# Revit family: RN 41133 Rubinetto da giardino
name_source: partatom
category: Rohrzubehör
units: mm (PartAtom-declared; Revit-internal decimal feet)

## family parameters
Arbeitsebenenbasiert = Nein
Beim Laden mit Abzugskörper schneiden = Nein
Bemaßung runder Anschluss = Durchmesser verwenden
Gemeinsam genutzt = Nein
Immer vertikal = Ja
Teiletyp = Ventil - Zerlegung in

## types (4) — shared parameters
1.010.00.2 Blattnummer der Richtlinie = 17
1.010.00.3 Ausgabedatum (Monat) der Richtlinie = 201601
1.010.00.4 Herstellername = R. Nussbaum AG
1.010.00.5 Revisionsdatum der Datei = 20190528
1.010.00.6 Webadresse des Herstellers = http://www.nussbaum.ch
1.100.00.3 Sortiernummer für Anzeigereihenfolge = 3
1.100.00.4 Produktbezeichnung = Entnahmearmaturen
1.960/3L.00.8 Link (URL) = https://www.nussbaum.ch
17.700.00.4 Armaturentyp = 4
17.700.00.6 kvs-Wert [m3/h] = 2.1
17.700.00.7 Maximale Betriebstemperatur TB [°C] = 90
17.700.00.8 Maximaler Betriebsdruck (Arbeitsdruck) ps [1.0 · 105 Pa] = 16
CONNECTOR0_dX_00 = 128 mm
CONNECTOR0_dX_01 = 103 mm
CONNECTOR0_ref_dX = 128 mm
Connector Visibility = Nein
EnclosingSpace Visibility = Nein
Hersteller = R. Nussbauzm AG
URL = https://www.nussbaum.ch

## per-type parameters (varying)
| type | 1.800.00.3 TGA-Nummer | 1.810.00.3 Hersteller-Bestellnummer | 1.810.00.4 DATANORM-Nummer | 1.810.00.6 GTIN-Nummer | 17.700.00.30 Produktbeschreibung | 17.700.00.5 Nennweite DN | CONNECTOR0_DIAMETER_dX_0r | CONNECTOR1_DIAMETER_dNBN0_0r | CONNECTOR1_dNBN0_00 | CONNECTOR1_dNBN0_01 | CONNECTOR1_ref_dNBN0 | Modell | R. Nussbaum AG 41133.04 de Visibility | R. Nussbaum AG 41133.05 de Visibility | R. Nussbaum AG 41133.54 de Visibility | R. Nussbaum AG 41133.55 de Visibility | Typenkommentare |
| DN 15 | 00302300000000000000000000000200700000000000000001???00000 | 41133.04 | 41133.04 | 7612945732743 | 41133.04, Gartenventil, mit Steckschlüssel, DN=15 | 15 | 15 mm | 20 mm | 48 mm | 38 mm | 38 mm | 41133.04 | Ja | Nein | Nein | Nein | Rubinetto da giardinoDN 15 |
| DN 20 1 | 00302300000000000000000000000200700000000000000002???00000 | 41133.05 | 41133.05 | 7612945732767 | 41133.05, Gartenventil, mit Steckschlüssel, DN=20 | 20 | 20 mm | 25 mm  [stored 0.082021 ft] | 52 mm | 41 mm | 41 mm | 41133.05 | Nein | Ja | Nein | Nein | Rubinetto da giardinoDN 20 1 |
| DN 15 1 | 00302300000000000000000000000200200000000000000003???00000 | 41133.54 | 41133.54 | 7612945732750 | 41133.54, Gartenventil, mit Steckschlüssel, DN=15 | 15 | 15 mm | 20 mm | 48 mm | 38 mm | 38 mm | 41133.54 | Nein | Nein | Ja | Nein | Rubinetto da giardinoDN 15 1 |
| DN 20 | 00302300000000000000000000000200200000000000000004???00000 | 41133.55 | 41133.55 | 7612945732866 | 41133.55, Gartenventil, mit Steckschlüssel, DN=20 | 20 | 20 mm | 25 mm  [stored 0.082021 ft] | 52 mm | 41 mm | 41 mm | 41133.55 | Nein | Nein | Nein | Ja | Rubinetto da giardinoDN 20 |

note: [stored X ft] marks values corroborated as IEEE doubles in the binary element streams (Revit-internal decimal feet)

## geometry (parser evidence)
native form markers: Sweep x1
no freeform markers — native parametric forms only
